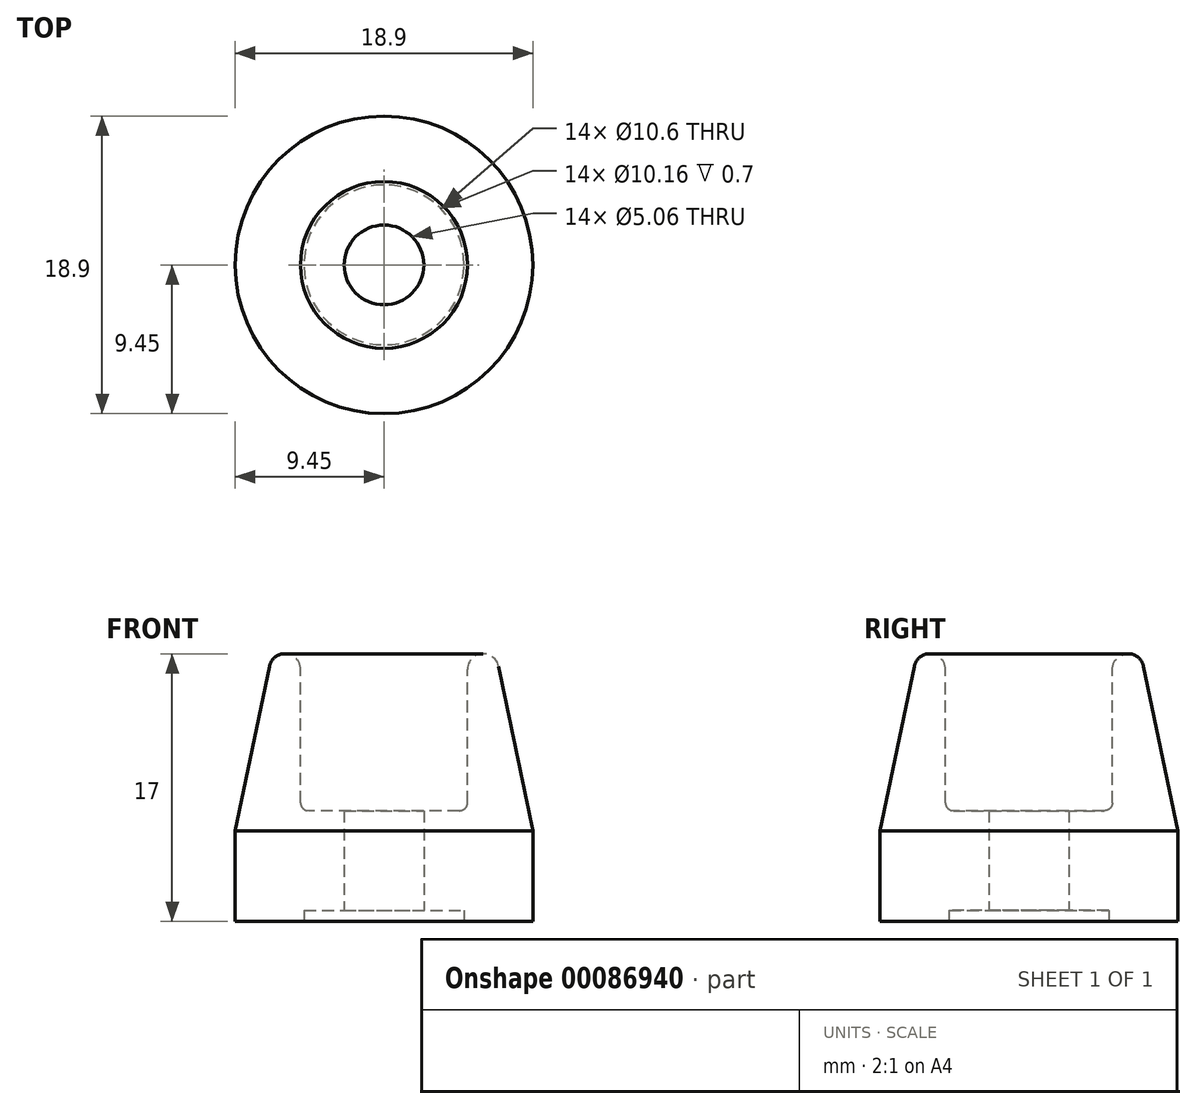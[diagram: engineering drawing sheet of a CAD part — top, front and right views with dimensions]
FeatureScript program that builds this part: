
annotation { "Feature Type Name" : "Feature", "Feature Type Description" : "" }
export const myFeature = defineFeature(function(context is Context, id is Id, definition is map)
    precondition{}
    {
        {
            var Q0;
            Q0=qCreatedBy(makeId("Front.planeOp"),FACE);
            var sketch = newSketch(context, id + "F0", { "sketchPlane" : qUnion([Q0])});
            skLineSegment(sketch, "E0", {"start": v(0, 0) * mm, "end": v(-9.45, 0) * mm});
            skLineSegment(sketch, "E1", {"start": v(-9.45, 0) * mm, "end": v(-9.45, 5.74) * mm});
            skLineSegment(sketch, "E2", {"start": v(0, 7.03) * mm, "end": v(0, 0) * mm});
            skLineSegment(sketch, "E3", {"start": v(-7.28, 16.2) * mm, "end": v(-9.45, 5.74) * mm});
            skArc(sketch, "E4.filletArc", {"start": v(-5.3, 16) * mm, "mid": v(-6.2, 17) * mm, "end": v(-7.28, 16.2) * mm});
            skLineSegment(sketch, "E5", {"start": v(-8.08, 17) * mm, "end": v(-3.93, 17) * mm, "construction": true});
            skLineSegment(sketch, "E6", {"start": v(-4.8, 7.03) * mm, "end": v(0, 7.03) * mm});
            skArc(sketch, "E7.filletArc", {"start": v(-5.3, 7.53) * mm, "mid": v(-5.15, 7.18) * mm, "end": v(-4.8, 7.03) * mm});
            skLineSegment(sketch, "E8", {"start": v(-5.3, 16) * mm, "end": v(-5.3, 7.53) * mm});
            skSolve(sketch);
        }
        {
            var Q0;
            Q0=makeQuery(id+"F0.imprint","IMPRINT",FACE,{"disambiguationData":[TD([[makeQuery(id+"F0.imprint","IMPRINT",EDGE,{"derivedFrom":sQuery(id+"F0.wireOp",EDGE,"E0")}),-1.0]])]});
            var Q1;
            Q1=sQuery(id+"F0.wireOp",EDGE,"E2");
            revolve(context, id + "F1", {"entities" : qUnion([Q0]), "axis" : qUnion([Q1]), "revolveType" : RevolveType.FULL});
        }
        {
            var Q0;
            Q0=makeQuery(id+"F1.opRevolve","SWEPT_FACE",FACE,{"disambiguationData":[OSD([sQuery(id+"F0.wireOp",EDGE,"E0")])]});
            var sketch = newSketch(context, id + "F2", { "sketchPlane" : qUnion([Q0])});
            skCircle(sketch, "E9", {"center": v(0, 0) * mm, "radius": 5.08 * mm});
            skSolve(sketch);
        }
        {
            var Q0;
            Q0=makeQuery(id+"F2.imprint","IMPRINT",FACE,{"disambiguationData":[TD([[makeQuery(id+"F2.imprint","IMPRINT",EDGE,{"derivedFrom":sQuery(id+"F2.wireOp",EDGE,"E9")}),1.0]])]});
            extrude(context, id + "F3", {"entities" : qUnion([Q0]), "operationType" : NewBodyOperationType.REMOVE, "oppositeDirection" : true, "depth" : .7 * mm});
        }
        {
            var Q0;
            Q0=makeQuery(id+"F3.boolean.opBoolean","COPY",FACE,{"derivedFrom":makeQuery(id+"F3.opExtrude","CAP_FACE",FACE,{"disambiguationData":[OSD([sQuery(id+"F2.wireOp",EDGE,"E9")])],"isStart":false})});
            var sketch = newSketch(context, id + "F4", { "sketchPlane" : qUnion([Q0])});
            skCircle(sketch, "E10", {"center": v(0, 0) * mm, "radius": 2.53 * mm});
            skSolve(sketch);
        }
        {
            var Q0;
            Q0=makeQuery(id+"F4.imprint","IMPRINT",FACE,{"disambiguationData":[TD([[makeQuery(id+"F4.imprint","IMPRINT",EDGE,{"derivedFrom":sQuery(id+"F4.wireOp",EDGE,"E10")}),1.0]])]});
            extrude(context, id + "F5", {"entities" : qUnion([Q0]), "operationType" : NewBodyOperationType.REMOVE, "oppositeDirection" : true, "depth" : 25 * mm});
        }
    });
